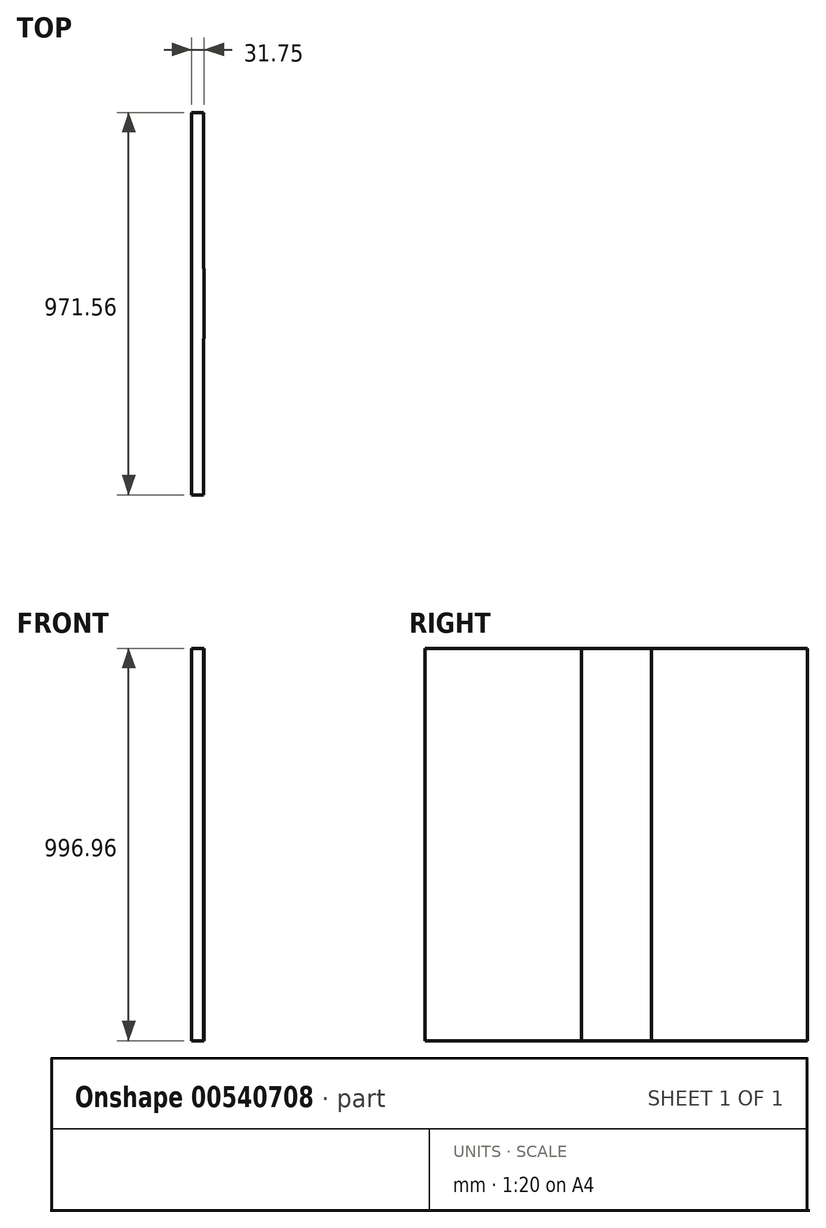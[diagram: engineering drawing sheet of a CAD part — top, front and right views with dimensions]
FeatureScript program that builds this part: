
annotation { "Feature Type Name" : "Feature", "Feature Type Description" : "" }
export const myFeature = defineFeature(function(context is Context, id is Id, definition is map)
    precondition{}
    {
        {
            var Q0;
            Q0=qCreatedBy(makeId("Right.planeOp"),FACE);
            var sketch = newSketch(context, id + "F0", { "sketchPlane" : qUnion([Q0])});
            skLineSegment(sketch, "E0.bottom", {"start": v(485.77, 498.48) * mm, "end": v(-485.78, 498.48) * mm});
            skLineSegment(sketch, "E0.top", {"start": v(485.78, -498.48) * mm, "end": v(-485.77, -498.48) * mm});
            skLineSegment(sketch, "E0.left", {"start": v(485.77, 498.48) * mm, "end": v(485.78, -498.47) * mm});
            skLineSegment(sketch, "E0.right", {"start": v(-485.78, 498.48) * mm, "end": v(-485.77, -498.48) * mm});
            skPoint(sketch, "E0.middle", {"position": v(0, 0) * mm});
            skSolve(sketch);
        }
        {
            var Q0;
            Q0=makeQuery(id+"F0.imprint","IMPRINT",FACE,{"disambiguationData":[TD([[makeQuery(id+"F0.imprint","IMPRINT",EDGE,{"derivedFrom":sQuery(id+"F0.wireOp",EDGE,"E0.bottom")}),1.0]])]});
            extrude(context, id + "F1", {"entities" : qUnion([Q0]), "depth" : 30.23 * mm, "offsetDistance" : 25.4 * mm});
        }
        {
            var Q0;
            Q0=makeQuery(id+"F1.opExtrude","CAP_FACE",FACE,{"disambiguationData":[OSD([sQuery(id+"F0.wireOp",EDGE,"E0.bottom"),sQuery(id+"F0.wireOp",EDGE,"E0.top"),sQuery(id+"F0.wireOp",EDGE,"E0.left"),sQuery(id+"F0.wireOp",EDGE,"E0.right")])],"isStart":false});
            var sketch = newSketch(context, id + "F2", { "sketchPlane" : qUnion([Q0])});
            skLineSegment(sketch, "E1.bottom", {"start": v(88.9, 498.48) * mm, "end": v(-88.9, 498.48) * mm});
            skLineSegment(sketch, "E1.top", {"start": v(88.9, -498.48) * mm, "end": v(-88.9, -498.48) * mm});
            skLineSegment(sketch, "E1.left", {"start": v(88.9, 498.48) * mm, "end": v(88.9, -498.48) * mm});
            skLineSegment(sketch, "E1.right", {"start": v(-88.9, 498.48) * mm, "end": v(-88.9, -498.48) * mm});
            skPoint(sketch, "E1.middle", {"position": v(0, 0) * mm});
            skSolve(sketch);
        }
        {
            var Q0;
            Q0 = qSketchRegion(id + "F2", true);
            extrude(context, id + "F3", {"entities" : qUnion([Q0]), "operationType" : NewBodyOperationType.ADD, "depth" : 1.52 * mm, "offsetDistance" : 25.4 * mm});
        }
    });
